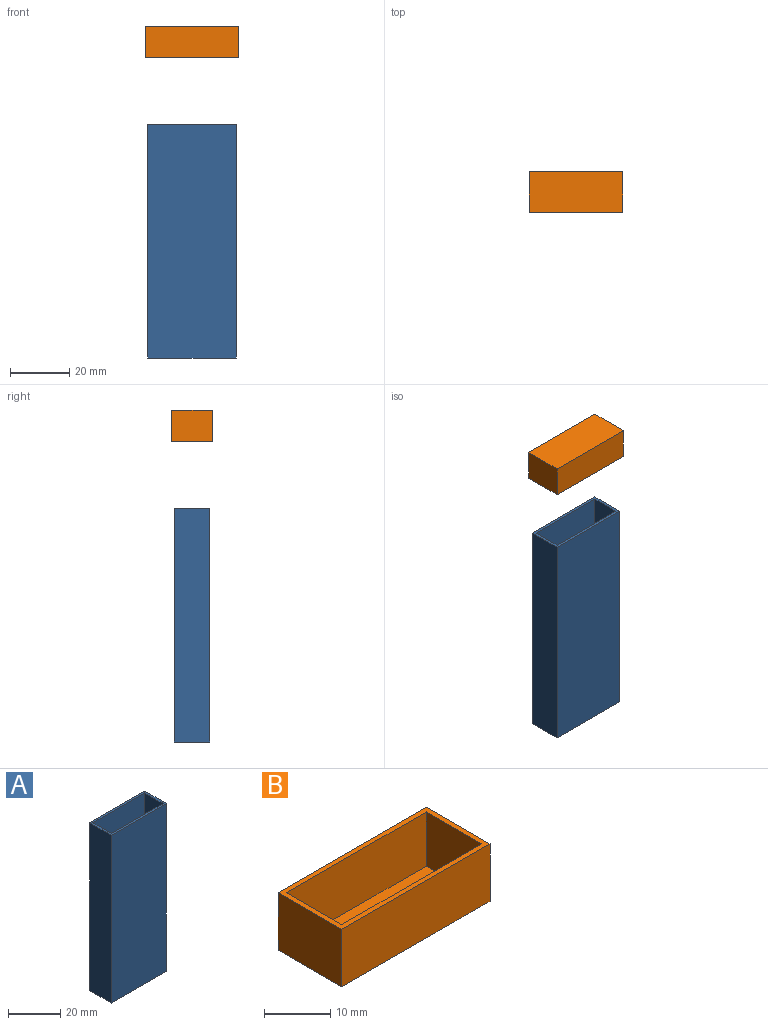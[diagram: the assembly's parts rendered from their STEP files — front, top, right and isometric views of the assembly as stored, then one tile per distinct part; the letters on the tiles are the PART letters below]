
ASSEMBLY  parts=2 mates=1
PART A: 11 faces, bbox 29.8x11.8x78.6 mm
  f0: plane 78.6x29.8mm, normal (0,1,0), area 2342.3mm2, adj f1,f3,f4,f9
  f1: plane 78.6x11.8mm, normal (-1,0,0), area 927.5mm2, adj f0,f2,f4,f9
  f2: plane 78.6x29.8mm, normal (0,-1,0), area 2342.3mm2, adj f1,f3,f4,f9
  f3: plane 78.6x11.8mm, normal (1,0,0), area 927.5mm2, adj f0,f2,f4,f9
  f4: plane 29.8x11.8mm, normal (0,0,-1), area 351.6mm2, adj f0,f1,f2,f3
  f5: plane 78x28mm, normal (0,1,0), area 2184mm2, adj f6,f8,f9,f10
  f6: plane 78x10mm, normal (1,0,0), area 780mm2, adj f5,f7,f9,f10
  f7: plane 78x28mm, normal (0,-1,0), area 2184mm2, adj f6,f8,f9,f10
  f8: plane 78x10mm, normal (-1,0,0), area 780mm2, adj f5,f7,f9,f10
  f9: plane 29.8x11.8mm, normal (0,0,1), area 71.6mm2, adj f0,f1,f2,f3,f5,f6,f7,f8
  f10: plane 28x10mm, normal (0,0,1), area 280mm2, adj f5,f6,f7,f8
PART B: 11 faces, bbox 31.6x13.6x10.6 mm
  f0: plane 31.6x10.6mm, normal (0,1,0), area 335mm2, adj f1,f3,f4,f9
  f1: plane 13.6x10.6mm, normal (-1,0,0), area 144.2mm2, adj f0,f2,f4,f9
  f2: plane 31.6x10.6mm, normal (0,-1,0), area 335mm2, adj f1,f3,f4,f9
  f3: plane 13.6x10.6mm, normal (1,0,0), area 144.2mm2, adj f0,f2,f4,f9
  f4: plane 31.6x13.6mm, normal (0,0,-1), area 429.8mm2, adj f0,f1,f2,f3
  f5: plane 29.8x10mm, normal (0,1,0), area 298mm2, adj f6,f8,f9,f10
  f6: plane 11.8x10mm, normal (1,0,0), area 118mm2, adj f5,f7,f9,f10
  f7: plane 29.8x10mm, normal (0,-1,0), area 298mm2, adj f6,f8,f9,f10
  f8: plane 11.8x10mm, normal (-1,0,0), area 118mm2, adj f5,f7,f9,f10
  f9: plane 31.6x13.6mm, normal (0,0,1), area 78.1mm2, adj f0,f1,f2,f3,f5,f6,f7,f8
  f10: plane 29.8x11.8mm, normal (0,0,1), area 351.6mm2, adj f5,f6,f7,f8
PLACE A rot(axis=(0,0,-1),0deg) t=(15.86,-7.78,-87.05)mm
PLACE B rot(axis=(0,1,0),180deg) t=(12.01,9.95,23.59)mm
MATE slider A.f9 <-> B.f10  axis (0,0,1) through (15.67,-7.57,-9.05)mm
